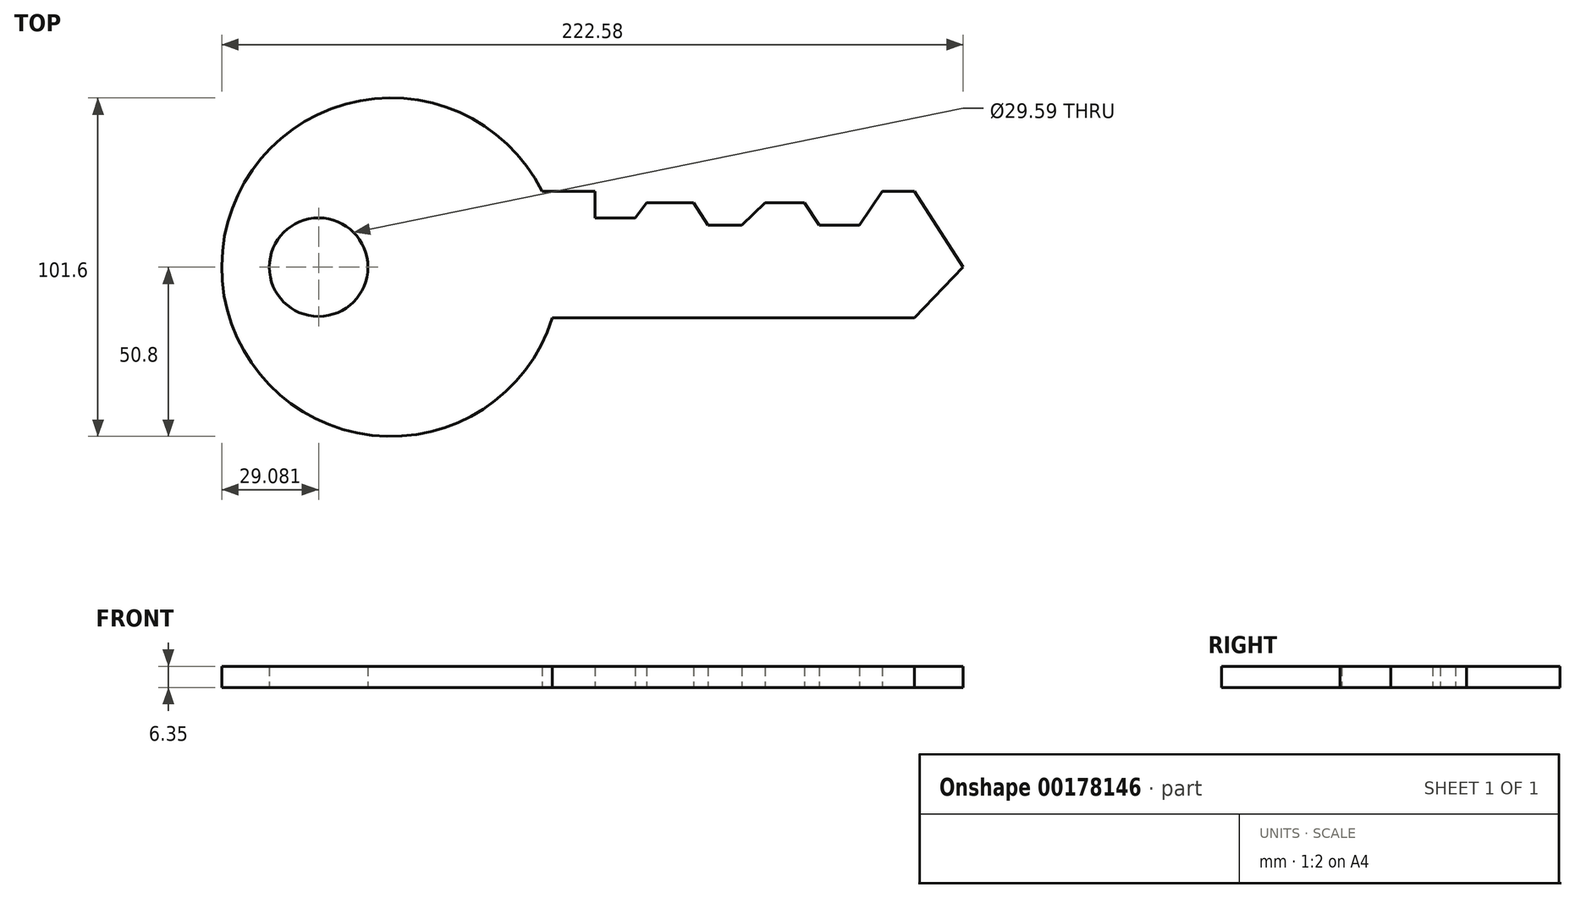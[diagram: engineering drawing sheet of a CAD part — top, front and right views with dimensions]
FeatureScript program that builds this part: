
annotation { "Feature Type Name" : "Feature", "Feature Type Description" : "" }
export const myFeature = defineFeature(function(context is Context, id is Id, definition is map)
    precondition{}
    {
        {
            var Q0;
            Q0=qCreatedBy(makeId("Top.planeOp"),FACE);
            var sketch = newSketch(context, id + "F0", { "sketchPlane" : qUnion([Q0])});
            skCircle(sketch, "E0", {"center": v(-68.6, 0) * mm, "radius": 50.8 * mm});
            skLineSegment(sketch, "E1.bottom", {"start": v(-27.2, -15.26) * mm, "end": v(88.56, -15.26) * mm});
            skLineSegment(sketch, "E1.top", {"start": v(-27.2, 22.78) * mm, "end": v(88.56, 22.78) * mm});
            skLineSegment(sketch, "E1.left", {"start": v(-27.2, -15.26) * mm, "end": v(-27.2, 22.78) * mm});
            skPoint(sketch, "E2", {"position": v(103.17, 0) * mm});
            skLineSegment(sketch, "E3", {"start": v(88.56, 22.78) * mm, "end": v(103.17, 0) * mm});
            skLineSegment(sketch, "E4", {"start": v(88.56, -15.26) * mm, "end": v(103.17, 0) * mm});
            skLineSegment(sketch, "E5", {"start": v(78.92, 22.78) * mm, "end": v(72.02, 12.58) * mm});
            skLineSegment(sketch, "E6", {"start": v(72.02, 12.58) * mm, "end": v(59.9, 12.58) * mm});
            skLineSegment(sketch, "E7", {"start": v(59.9, 12.58) * mm, "end": v(55.53, 19.39) * mm});
            skLineSegment(sketch, "E8", {"start": v(55.53, 19.39) * mm, "end": v(43.63, 19.39) * mm});
            skLineSegment(sketch, "E9", {"start": v(43.63, 19.39) * mm, "end": v(36.74, 12.58) * mm});
            skLineSegment(sketch, "E10", {"start": v(36.74, 12.58) * mm, "end": v(26.54, 12.58) * mm});
            skLineSegment(sketch, "E11", {"start": v(26.54, 12.58) * mm, "end": v(22.18, 19.39) * mm});
            skLineSegment(sketch, "E12", {"start": v(22.18, 19.39) * mm, "end": v(8.08, 19.39) * mm});
            skLineSegment(sketch, "E13", {"start": v(8.08, 19.39) * mm, "end": v(4.76, 14.8) * mm});
            skLineSegment(sketch, "E14", {"start": v(4.76, 14.8) * mm, "end": v(-7.36, 14.8) * mm});
            skLineSegment(sketch, "E15", {"start": v(-7.36, 14.8) * mm, "end": v(-7.36, 22.78) * mm});
            skLineSegment(sketch, "E16", {"start": v(-68.6, 0) * mm, "end": v(-119.4, 0) * mm, "construction": true});
            skCircle(sketch, "E17", {"center": v(-90.33, 0) * mm, "radius": 14.8 * mm});
            skSolve(sketch);
        }
        {
            var Q0;
            {var subQ0=sQuery(id+"F0.wireOp",EDGE,"E1.left");Q0=makeQuery(id+"F0.imprint","IMPRINT",FACE,{"disambiguationData":[TD([[makeQuery(id+"F0.imprint","IMPRINT",EDGE,{"derivedFrom":subQ0}),1.0]])]});}
            var Q1;
            {var subQ1=sQuery(id+"F0.wireOp",EDGE,"E3");Q1=makeQuery(id+"F0.imprint","IMPRINT",FACE,{"disambiguationData":[TD([[makeQuery(id+"F0.imprint","IMPRINT",EDGE,{"derivedFrom":subQ1}),-1.0]])]});}
            var Q2;
            {var subQ5=sQuery(id+"F0.wireOp",EDGE,"E1.left");Q2=makeQuery(id+"F0.imprint","IMPRINT",FACE,{"disambiguationData":[TD([[makeQuery(id+"F0.imprint","IMPRINT",EDGE,{"derivedFrom":subQ5}),-1.0]])]});}
            extrude(context, id + "F1", {"entities" : qUnion([Q0, Q1, Q2]), "depth" : 6.35 * mm});
        }
    });
